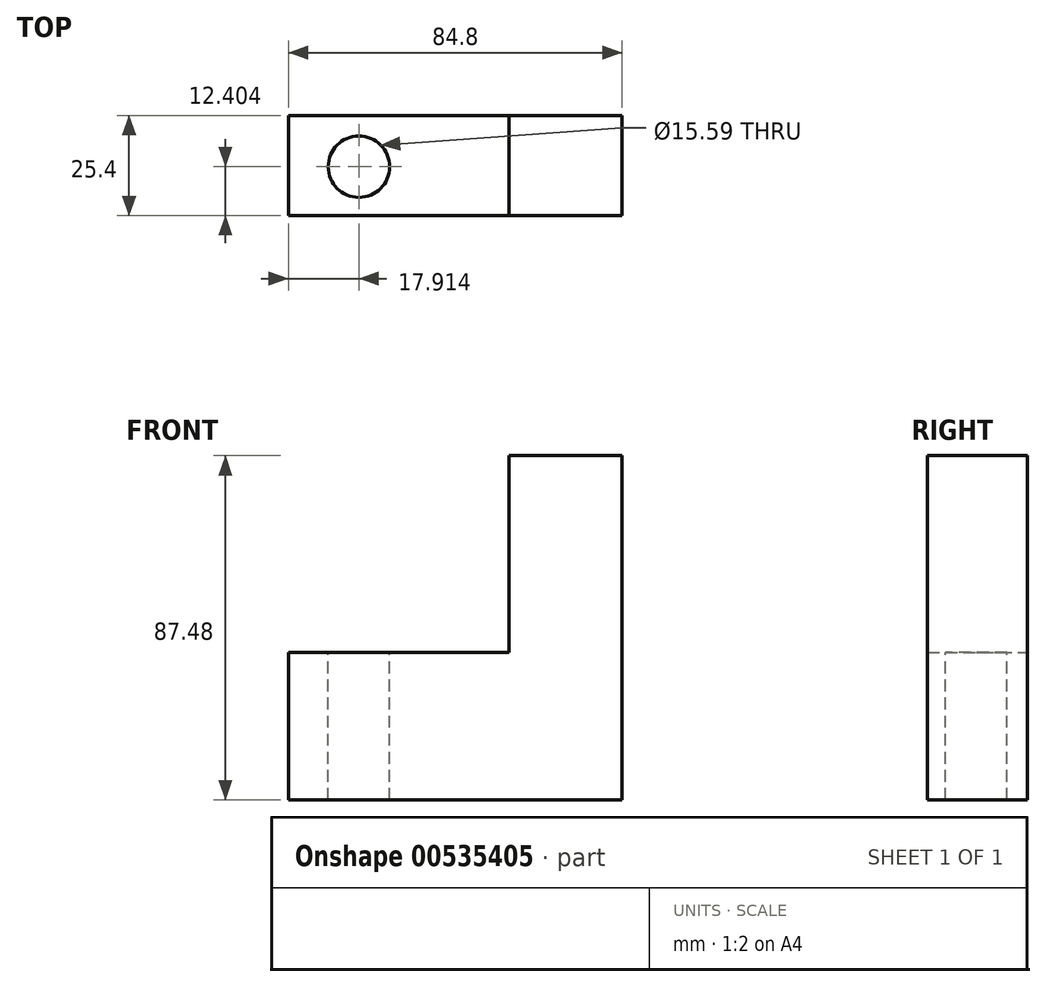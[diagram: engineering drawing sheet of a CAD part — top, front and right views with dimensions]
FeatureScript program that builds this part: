
annotation { "Feature Type Name" : "Feature", "Feature Type Description" : "" }
export const myFeature = defineFeature(function(context is Context, id is Id, definition is map)
    precondition{}
    {
        {
            var Q0;
            Q0=qCreatedBy(makeId("Front.planeOp"),FACE);
            var sketch = newSketch(context, id + "F0", { "sketchPlane" : qUnion([Q0])});
            skLineSegment(sketch, "E0.bottom", {"start": v(-56.01, -37.5) * mm, "end": v(28.79, -37.5) * mm});
            skLineSegment(sketch, "E0.top", {"start": v(-56.01, 0) * mm, "end": v(28.79, 0) * mm});
            skLineSegment(sketch, "E0.left", {"start": v(-56.01, -37.5) * mm, "end": v(-56.01, 0) * mm});
            skLineSegment(sketch, "E0.right", {"start": v(28.79, -37.5) * mm, "end": v(28.79, 0) * mm});
            skLineSegment(sketch, "E1.bottom", {"start": v(0, 49.97) * mm, "end": v(28.79, 49.97) * mm});
            skLineSegment(sketch, "E1.top", {"start": v(0, 0) * mm, "end": v(28.79, 0) * mm});
            skLineSegment(sketch, "E1.left", {"start": v(0, 49.97) * mm, "end": v(0, 0) * mm});
            skLineSegment(sketch, "E1.right", {"start": v(28.79, 49.97) * mm, "end": v(28.79, 0) * mm});
            skSolve(sketch);
        }
        {
            var Q0;
            Q0=makeQuery(id+"F0.imprint","IMPRINT",FACE,{"disambiguationData":[TD([[makeQuery(id+"F0.imprint","IMPRINT",EDGE,{"derivedFrom":sQuery(id+"F0.wireOp",EDGE,"E1.bottom")}),-1.0]])]});
            extrude(context, id + "F1", {"entities" : qUnion([Q0]), "depth" : 25.4 * mm, "offsetDistance" : 25.4 * mm});
        }
        {
            var Q0;
            Q0=makeQuery(id+"F0.imprint","IMPRINT",FACE,{"disambiguationData":[TD([[makeQuery(id+"F0.imprint","IMPRINT",EDGE,{"derivedFrom":sQuery(id+"F0.wireOp",EDGE,"E1.bottom")}),-1.0]])]});
            var Q1;
            Q1=makeQuery(id+"F0.imprint","IMPRINT",FACE,{"disambiguationData":[TD([[makeQuery(id+"F0.imprint","IMPRINT",EDGE,{"derivedFrom":sQuery(id+"F0.wireOp",EDGE,"E0.bottom")}),1.0]])]});
            extrude(context, id + "F2", {"entities" : qUnion([Q0, Q1]), "operationType" : NewBodyOperationType.ADD, "depth" : 25.4 * mm, "offsetDistance" : 25.4 * mm});
        }
        {
            var Q0;
            Q0=makeQuery(id+"F1.opExtrude","SWEPT_FACE",FACE,{"disambiguationData":[OSD([sQuery(id+"F0.wireOp",EDGE,"E1.left")])]});
            extrude(context, id + "F3", {"entities" : qUnion([Q0]), "operationType" : NewBodyOperationType.REMOVE, "oppositeDirection" : true, "depth" : 25.4 * mm, "offsetDistance" : 25.4 * mm});
        }
        {
            var Q0;
            Q0=makeQuery(id+"F0.imprint","IMPRINT",FACE,{"disambiguationData":[TD([[makeQuery(id+"F0.imprint","IMPRINT",EDGE,{"derivedFrom":sQuery(id+"F0.wireOp",EDGE,"E1.bottom")}),-1.0]])]});
            extrude(context, id + "F4", {"entities" : qUnion([Q0]), "operationType" : NewBodyOperationType.ADD, "depth" : 25.4 * mm, "offsetDistance" : 25.4 * mm});
        }
        {
            var Q0;
            {var subQ0=sQuery(id+"F0.wireOp",EDGE,"E0.top");Q0=makeQuery(id+"F3.boolean.opBoolean","MERGE",FACE,{"derivedFrom":[makeQuery(id+"F2.opExtrude","SWEPT_FACE",FACE,{"disambiguationData":[OSD([subQ0])]}),makeQuery(id+"F3.opExtrude","SWEPT_FACE",FACE,{"disambiguationData":[OSD([subQ0,sQuery(id+"F0.wireOp",EDGE,"E1.top"),sQuery(id+"F0.wireOp",EDGE,"E1.left")])]})]});}
            var sketch = newSketch(context, id + "F5", { "sketchPlane" : qUnion([Q0])});
            skCircle(sketch, "E2", {"center": v(-38.1, -13) * mm, "radius": 7.8 * mm});
            skPoint(sketch, "E2.first.point", {"position": v(-30.3, -13.32) * mm});
            skPoint(sketch, "E2.second.point", {"position": v(-45.88, -12.66) * mm});
            skPoint(sketch, "E2.third.point", {"position": v(-38.1, -5.2) * mm});
            skSolve(sketch);
        }
        {
            var Q0;
            Q0=makeQuery(id+"F5.imprint","IMPRINT",FACE,{"disambiguationData":[TD([[makeQuery(id+"F5.imprint","IMPRINT",EDGE,{"derivedFrom":sQuery(id+"F5.wireOp",EDGE,"E2")}),1.0]])]});
            extrude(context, id + "F6", {"entities" : qUnion([Q0]), "operationType" : NewBodyOperationType.REMOVE, "oppositeDirection" : true, "depth" : 38.1 * mm, "offsetDistance" : 25.4 * mm});
        }
    });
